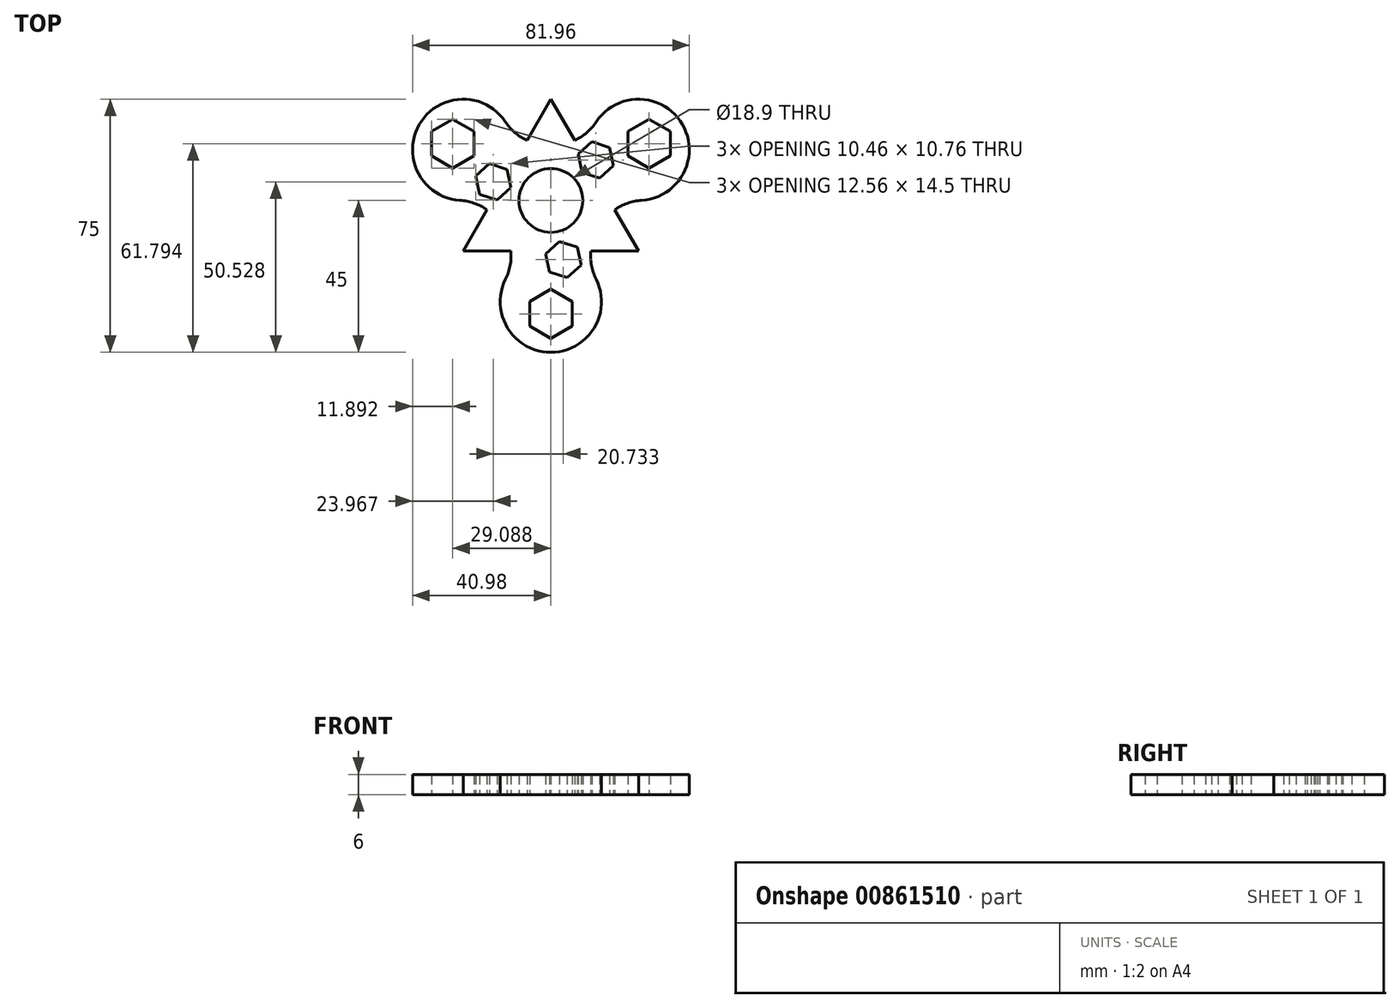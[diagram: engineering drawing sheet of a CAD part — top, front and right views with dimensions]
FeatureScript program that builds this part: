
annotation { "Feature Type Name" : "Feature", "Feature Type Description" : "" }
export const myFeature = defineFeature(function(context is Context, id is Id, definition is map)
    precondition{}
    {
        {
            var Q0;
            Q0=qCreatedBy(makeId("Top.planeOp"),FACE);
            var sketch = newSketch(context, id + "F0", { "sketchPlane" : qUnion([Q0])});
            skCircle(sketch, "E0.cCircle", {"center": v(0, 0) * mm, "radius": 15 * mm, "construction": true});
            skLineSegment(sketch, "E0.0", {"start": v(25.98, -15) * mm, "end": v(-25.98, -15) * mm});
            skLineSegment(sketch, "E0.1", {"start": v(-25.98, -15) * mm, "end": v(0, 30) * mm});
            skLineSegment(sketch, "E0.2", {"start": v(0, 30) * mm, "end": v(25.98, -15) * mm});
            skPoint(sketch, "E0.0.midPoint", {"position": v(0, -15) * mm});
            skCircle(sketch, "E1", {"center": v(0, 0) * mm, "radius": 9.45 * mm});
            skLineSegment(sketch, "E2", {"start": v(0, 0) * mm, "end": v(58.18, 33.59) * mm, "construction": true});
            skCircle(sketch, "E3", {"center": v(25.98, 15) * mm, "radius": 15 * mm});
            skLineSegment(sketch, "E4", {"start": v(-65.68, 30) * mm, "end": v(68.7, 30) * mm, "construction": true});
            skPoint(sketch, "E5", {"position": v(13.47, 23.27) * mm});
            skPoint(sketch, "E6", {"position": v(7.06, 17.77) * mm});
            skArc(sketch, "E7", {"start": v(7.06, 17.77) * mm, "mid": v(10.65, 20.08) * mm, "end": v(13.47, 23.27) * mm});
            skArc(sketch, "E8.MirrorCS", {"start": v(18.92, -2.77) * mm, "mid": v(22.7, -0.82) * mm, "end": v(26.89, 0.03) * mm});
            skArc(sketch, "E9", {"start": v(26.89, 0.03) * mm, "mid": v(38.97, 22.5) * mm, "end": v(13.47, 23.27) * mm});
            skArc(sketch, "E10.1.0", {"start": v(-18.92, -2.77) * mm, "mid": v(-22.7, -0.82) * mm, "end": v(-26.89, 0.03) * mm});
            skCircle(sketch, "E10.1.1", {"center": v(-25.98, 15) * mm, "radius": 15 * mm});
            skArc(sketch, "E10.1.2", {"start": v(-7.06, 17.77) * mm, "mid": v(-10.65, 20.08) * mm, "end": v(-13.47, 23.27) * mm});
            skArc(sketch, "E10.2.0", {"start": v(11.86, -15) * mm, "mid": v(12.06, -19.26) * mm, "end": v(13.42, -23.3) * mm});
            skCircle(sketch, "E10.2.1", {"center": v(0, -30) * mm, "radius": 15 * mm});
            skArc(sketch, "E10.2.2", {"start": v(-11.86, -15) * mm, "mid": v(-12.06, -19.26) * mm, "end": v(-13.42, -23.3) * mm});
            skCircle(sketch, "E11.cCircle", {"center": v(29.09, 16.8) * mm, "radius": 7.25 * mm, "construction": true});
            skLineSegment(sketch, "E11.0", {"start": v(35.37, 20.42) * mm, "end": v(35.37, 13.17) * mm});
            skLineSegment(sketch, "E11.1", {"start": v(35.37, 13.17) * mm, "end": v(29.09, 9.54) * mm});
            skLineSegment(sketch, "E11.2", {"start": v(29.09, 9.54) * mm, "end": v(22.8, 13.17) * mm});
            skLineSegment(sketch, "E11.3", {"start": v(22.8, 13.17) * mm, "end": v(22.8, 20.42) * mm});
            skLineSegment(sketch, "E11.4", {"start": v(22.8, 20.42) * mm, "end": v(29.09, 24.04) * mm});
            skLineSegment(sketch, "E11.5", {"start": v(29.09, 24.04) * mm, "end": v(35.37, 20.42) * mm});
            skLineSegment(sketch, "E12", {"start": v(0, 0) * mm, "end": v(37.12, 33.43) * mm, "construction": true});
            skCircle(sketch, "E13.cCircle", {"center": v(13.3, 11.97) * mm, "radius": 5.5 * mm, "construction": true});
            skLineSegment(sketch, "E13.0", {"start": v(17.38, 15.65) * mm, "end": v(18.52, 10.27) * mm});
            skLineSegment(sketch, "E13.1", {"start": v(18.52, 10.27) * mm, "end": v(14.44, 6.6) * mm});
            skLineSegment(sketch, "E13.2", {"start": v(14.44, 6.6) * mm, "end": v(9.2, 8.29) * mm});
            skLineSegment(sketch, "E13.3", {"start": v(9.2, 8.29) * mm, "end": v(8.06, 13.67) * mm});
            skLineSegment(sketch, "E13.4", {"start": v(8.06, 13.67) * mm, "end": v(12.15, 17.35) * mm});
            skLineSegment(sketch, "E13.5", {"start": v(12.15, 17.35) * mm, "end": v(17.38, 15.65) * mm});
            skLineSegment(sketch, "E14.1.0", {"start": v(-35.37, 20.42) * mm, "end": v(-29.09, 24.04) * mm});
            skLineSegment(sketch, "E14.1.1", {"start": v(-35.37, 13.17) * mm, "end": v(-35.37, 20.42) * mm});
            skLineSegment(sketch, "E14.1.2", {"start": v(-29.09, 9.54) * mm, "end": v(-35.37, 13.17) * mm});
            skLineSegment(sketch, "E14.1.3", {"start": v(-22.8, 13.17) * mm, "end": v(-29.09, 9.54) * mm});
            skLineSegment(sketch, "E14.1.4", {"start": v(-22.8, 20.42) * mm, "end": v(-22.8, 13.17) * mm});
            skLineSegment(sketch, "E14.1.5", {"start": v(-21.1, 1.85) * mm, "end": v(-22.24, 7.23) * mm});
            skLineSegment(sketch, "E14.1.6", {"start": v(-22.24, 7.23) * mm, "end": v(-18.16, 10.9) * mm});
            skLineSegment(sketch, "E14.1.7", {"start": v(-18.16, 10.9) * mm, "end": v(-12.93, 9.2) * mm});
            skLineSegment(sketch, "E14.1.8", {"start": v(-12.93, 9.2) * mm, "end": v(-11.78, 3.83) * mm});
            skLineSegment(sketch, "E14.1.9", {"start": v(-11.78, 3.83) * mm, "end": v(-15.87, 0.15) * mm});
            skLineSegment(sketch, "E14.1.10", {"start": v(-15.87, 0.15) * mm, "end": v(-21.1, 1.85) * mm});
            skLineSegment(sketch, "E14.2.0", {"start": v(0, -40.84) * mm, "end": v(-6.28, -37.21) * mm});
            skLineSegment(sketch, "E14.2.1", {"start": v(6.28, -37.21) * mm, "end": v(0, -40.84) * mm});
            skLineSegment(sketch, "E14.2.2", {"start": v(6.28, -29.96) * mm, "end": v(6.28, -37.21) * mm});
            skLineSegment(sketch, "E14.2.3", {"start": v(0, -26.34) * mm, "end": v(6.28, -29.96) * mm});
            skLineSegment(sketch, "E14.2.4", {"start": v(-6.28, -29.96) * mm, "end": v(0, -26.34) * mm});
            skLineSegment(sketch, "E14.2.5", {"start": v(8.95, -19.2) * mm, "end": v(4.86, -22.88) * mm});
            skLineSegment(sketch, "E14.2.6", {"start": v(4.86, -22.88) * mm, "end": v(-0.37, -21.18) * mm});
            skLineSegment(sketch, "E14.2.7", {"start": v(-0.37, -21.18) * mm, "end": v(-1.51, -15.8) * mm});
            skLineSegment(sketch, "E14.2.8", {"start": v(-1.51, -15.8) * mm, "end": v(2.58, -12.12) * mm});
            skLineSegment(sketch, "E14.2.9", {"start": v(2.58, -12.12) * mm, "end": v(7.8, -13.82) * mm});
            skLineSegment(sketch, "E14.2.10", {"start": v(7.8, -13.82) * mm, "end": v(8.95, -19.2) * mm});
            skLineSegment(sketch, "E15.1.1", {"start": v(-29.09, 24.04) * mm, "end": v(-22.8, 20.42) * mm});
            skLineSegment(sketch, "E15.2.1", {"start": v(-6.28, -37.21) * mm, "end": v(-6.28, -29.96) * mm});
            skSolve(sketch);
        }
        {
            var Q0;
            {var subQ1=sQuery(id+"F0.wireOp",EDGE,"E10.1.1");var subQ4=sQuery(id+"F0.wireOp",EDGE,"E10.1.0");var subQ6=makeQuery(id+"F0.imprint","INTERSECT",VERTEX,{"disambiguationData":[OD(0.0)],"derivedFrom":[subQ4,subQ1]});Q0=makeQuery(id+"F0.imprint","IMPRINT",FACE,{"disambiguationData":[TD([[makeQuery(id+"F0.imprint","IMPRINT",EDGE,{"disambiguationData":[TD([[subQ6,1.0]])],"derivedFrom":subQ4}),-1.0]])]});}
            var Q1;
            {var subQ0=sQuery(id+"F0.wireOp",EDGE,"E10.1.2");var subQ1=sQuery(id+"F0.wireOp",EDGE,"E0.1");var subQ2=makeQuery(id+"F0.imprint","INTERSECT",VERTEX,{"derivedFrom":[subQ1,subQ0]});Q1=makeQuery(id+"F0.imprint","IMPRINT",FACE,{"disambiguationData":[TD([[makeQuery(id+"F0.imprint","IMPRINT",EDGE,{"disambiguationData":[TD([[subQ2,1.0]])],"derivedFrom":subQ1}),1.0]])]});}
            var Q2;
            {var subQ0=sQuery(id+"F0.wireOp",EDGE,"E10.1.0");var subQ1=sQuery(id+"F0.wireOp",EDGE,"E0.1");var subQ2=makeQuery(id+"F0.imprint","INTERSECT",VERTEX,{"derivedFrom":[subQ1,subQ0]});Q2=makeQuery(id+"F0.imprint","IMPRINT",FACE,{"disambiguationData":[TD([[makeQuery(id+"F0.imprint","IMPRINT",EDGE,{"disambiguationData":[TD([[subQ2,-1.0]])],"derivedFrom":subQ1}),1.0]])]});}
            var Q3;
            Q3=makeQuery(id+"F0.imprint","IMPRINT",FACE,{"disambiguationData":[TD([[makeQuery(id+"F0.imprint","IMPRINT",EDGE,{"derivedFrom":sQuery(id+"F0.wireOp",EDGE,"E1")}),-1.0]])]});
            var Q4;
            {var subQ0=sQuery(id+"F0.wireOp",EDGE,"E7");var subQ1=sQuery(id+"F0.wireOp",EDGE,"E0.2");var subQ2=makeQuery(id+"F0.imprint","INTERSECT",VERTEX,{"derivedFrom":[subQ1,subQ0]});Q4=makeQuery(id+"F0.imprint","IMPRINT",FACE,{"disambiguationData":[TD([[makeQuery(id+"F0.imprint","IMPRINT",EDGE,{"disambiguationData":[TD([[subQ2,-1.0]])],"derivedFrom":subQ1}),1.0]])]});}
            var Q5;
            {var subQ0=sQuery(id+"F0.wireOp",EDGE,"E7");var subQ1=sQuery(id+"F0.wireOp",EDGE,"E3");var subQ7=makeQuery(id+"F0.imprint","INTERSECT",VERTEX,{"disambiguationData":[OD(1.0)],"derivedFrom":[subQ1,subQ0]});Q5=makeQuery(id+"F0.imprint","IMPRINT",FACE,{"disambiguationData":[TD([[makeQuery(id+"F0.imprint","IMPRINT",EDGE,{"disambiguationData":[TD([[subQ7,-1.0]])],"derivedFrom":subQ1}),1.0]])]});}
            var Q6;
            {var subQ0=sQuery(id+"F0.wireOp",EDGE,"E8.MirrorCS");var subQ1=sQuery(id+"F0.wireOp",EDGE,"E0.2");var subQ2=makeQuery(id+"F0.imprint","INTERSECT",VERTEX,{"derivedFrom":[subQ1,subQ0]});Q6=makeQuery(id+"F0.imprint","IMPRINT",FACE,{"disambiguationData":[TD([[makeQuery(id+"F0.imprint","IMPRINT",EDGE,{"disambiguationData":[TD([[subQ2,1.0]])],"derivedFrom":subQ1}),1.0]])]});}
            var Q7;
            {var subQ0=sQuery(id+"F0.wireOp",EDGE,"E10.2.2");var subQ1=sQuery(id+"F0.wireOp",EDGE,"E0.0");var subQ2=makeQuery(id+"F0.imprint","INTERSECT",VERTEX,{"derivedFrom":[subQ1,subQ0]});Q7=makeQuery(id+"F0.imprint","IMPRINT",FACE,{"disambiguationData":[TD([[makeQuery(id+"F0.imprint","IMPRINT",EDGE,{"disambiguationData":[TD([[subQ2,1.0]])],"derivedFrom":subQ1}),1.0]])]});}
            var Q8;
            {var subQ1=sQuery(id+"F0.wireOp",EDGE,"E10.2.1");var subQ4=sQuery(id+"F0.wireOp",EDGE,"E10.2.0");var subQ6=makeQuery(id+"F0.imprint","INTERSECT",VERTEX,{"disambiguationData":[OD(0.0)],"derivedFrom":[subQ4,subQ1]});Q8=makeQuery(id+"F0.imprint","IMPRINT",FACE,{"disambiguationData":[TD([[makeQuery(id+"F0.imprint","IMPRINT",EDGE,{"disambiguationData":[TD([[subQ6,1.0]])],"derivedFrom":subQ4}),-1.0]])]});}
            var Q9;
            {var subQ0=sQuery(id+"F0.wireOp",EDGE,"E10.2.0");var subQ1=sQuery(id+"F0.wireOp",EDGE,"E0.0");var subQ2=makeQuery(id+"F0.imprint","INTERSECT",VERTEX,{"derivedFrom":[subQ1,subQ0]});Q9=makeQuery(id+"F0.imprint","IMPRINT",FACE,{"disambiguationData":[TD([[makeQuery(id+"F0.imprint","IMPRINT",EDGE,{"disambiguationData":[TD([[subQ2,-1.0]])],"derivedFrom":subQ1}),1.0]])]});}
            var Q10;
            {var subQ0=sQuery(id+"F0.wireOp",EDGE,"E10.1.1");var subQ1=makeQuery(id+"F0.imprint","INTERSECT",VERTEX,{"derivedFrom":[sQuery(id+"F0.wireOp",EDGE,"E10.1.0"),subQ0]});Q10=makeQuery(id+"F0.imprint","IMPRINT",FACE,{"disambiguationData":[TD([[makeQuery(id+"F0.imprint","IMPRINT",EDGE,{"disambiguationData":[TD([[subQ1,-1.0]])],"derivedFrom":subQ0}),1.0]])]});}
            var Q11;
            {var subQ0=sQuery(id+"F0.wireOp",EDGE,"E10.2.1");var subQ1=makeQuery(id+"F0.imprint","INTERSECT",VERTEX,{"derivedFrom":[sQuery(id+"F0.wireOp",EDGE,"E10.2.0"),subQ0]});Q11=makeQuery(id+"F0.imprint","IMPRINT",FACE,{"disambiguationData":[TD([[makeQuery(id+"F0.imprint","IMPRINT",EDGE,{"disambiguationData":[TD([[subQ1,-1.0]])],"derivedFrom":subQ0}),1.0]])]});}
            extrude(context, id + "F1", {"entities" : qUnion([Q0, Q1, Q2, Q3, Q4, Q5, Q6, Q7, Q8, Q9, Q10, Q11]), "depth" : 6 * mm, "offsetDistance" : 25 * mm});
        }
    });
